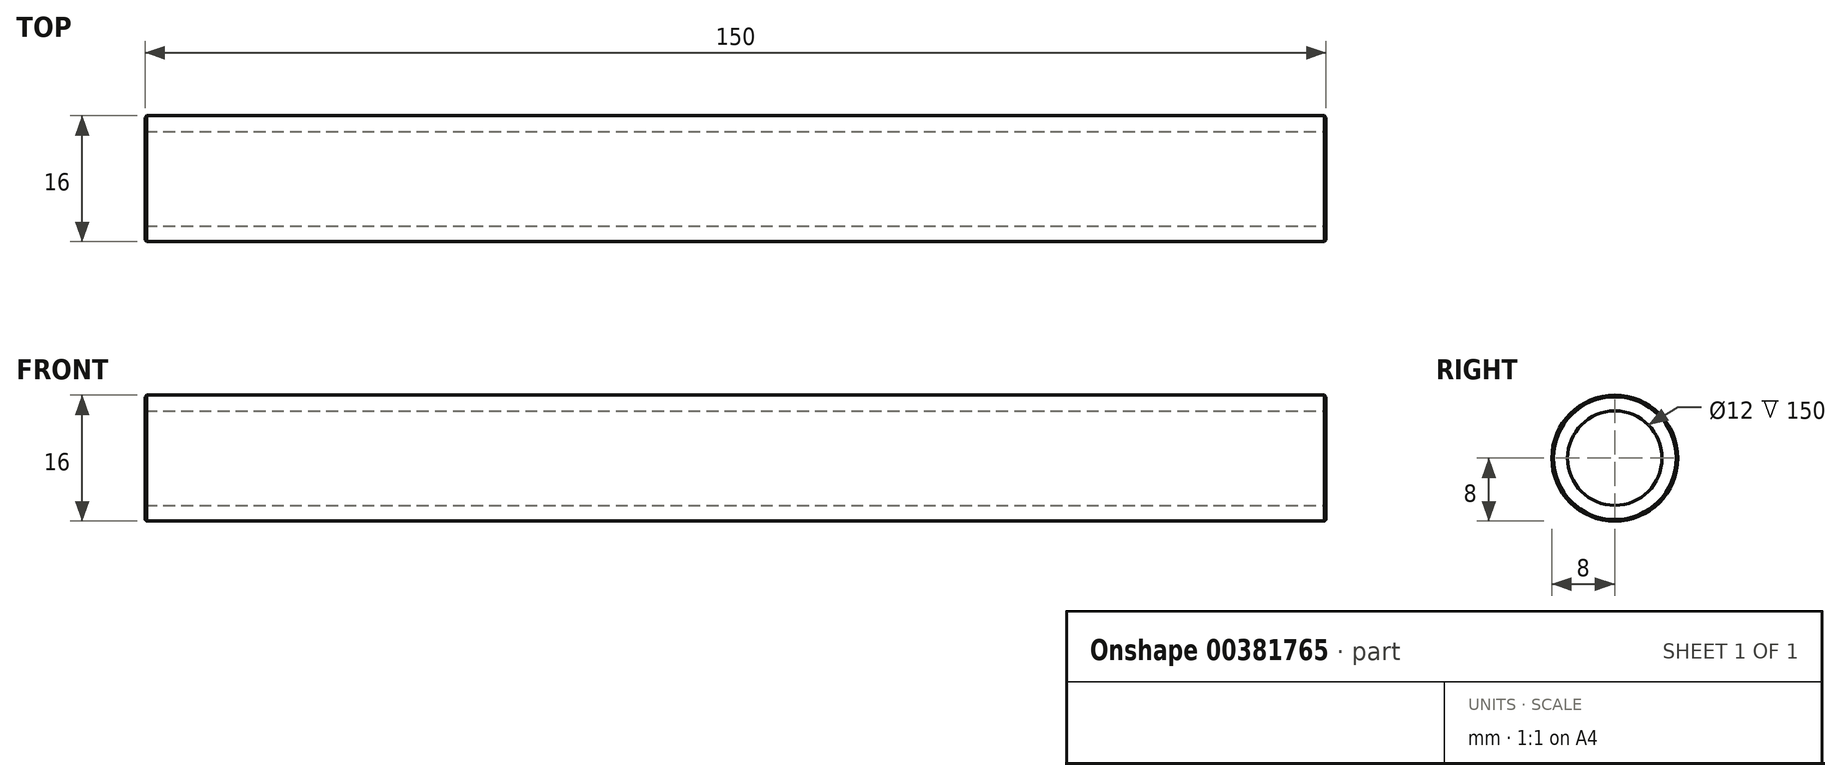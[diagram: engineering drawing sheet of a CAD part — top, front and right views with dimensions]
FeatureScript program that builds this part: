
annotation { "Feature Type Name" : "Feature", "Feature Type Description" : "" }
export const myFeature = defineFeature(function(context is Context, id is Id, definition is map)
    precondition{}
    {
        {
            var Q0;
            Q0=qCreatedBy(makeId("Right.planeOp"),FACE);
            var sketch = newSketch(context, id + "F0", { "sketchPlane" : qUnion([Q0])});
            skCircle(sketch, "E0", {"center": v(0, 0) * mm, "radius": 8 * mm});
            skSolve(sketch);
        }
        {
            var Q0;
            Q0 = qSketchRegion(id + "F0", true);
            extrude(context, id + "F1", {"entities" : qUnion([Q0]), "offsetDistance" : 25 * mm, "depth" : 150 * mm});
        }
        {
            var Q0;
            Q0=makeQuery(id+"F1.opExtrude","CAP_FACE",FACE,{"disambiguationData":[OSD([sQuery(id+"F0.wireOp",EDGE,"E0")])],"isStart":false});
            var sketch = newSketch(context, id + "F2", { "sketchPlane" : qUnion([Q0])});
            skCircle(sketch, "E1", {"center": v(0, 0) * mm, "radius": 6 * mm});
            skSolve(sketch);
        }
        {
            var Q0;
            Q0 = qSketchRegion(id + "F2", true);
            extrude(context, id + "F3", {"entities" : qUnion([Q0]), "operationType" : NewBodyOperationType.REMOVE, "endBound" : BoundingType.THROUGH_ALL, "oppositeDirection" : true, "depth" : 25 * mm});
        }
        {
            var Q0;
            Q0=makeQuery(id+"F1.opExtrude","CAP_EDGE",EDGE,{"disambiguationData":[OSD([sQuery(id+"F0.wireOp",EDGE,"E0")])],"isStart":false});
            chamfer(context, id + "F4", {"entities" : qUnion([Q0]), "width" : .2 * mm, "tangentPropagation" : true});
        }
        {
            var Q0;
            Q0=makeQuery(id+"F1.opExtrude","CAP_EDGE",EDGE,{"disambiguationData":[OSD([sQuery(id+"F0.wireOp",EDGE,"E0")])],"isStart":true});
            chamfer(context, id + "F5", {"entities" : qUnion([Q0]), "width" : .2 * mm, "tangentPropagation" : true});
        }
    });
